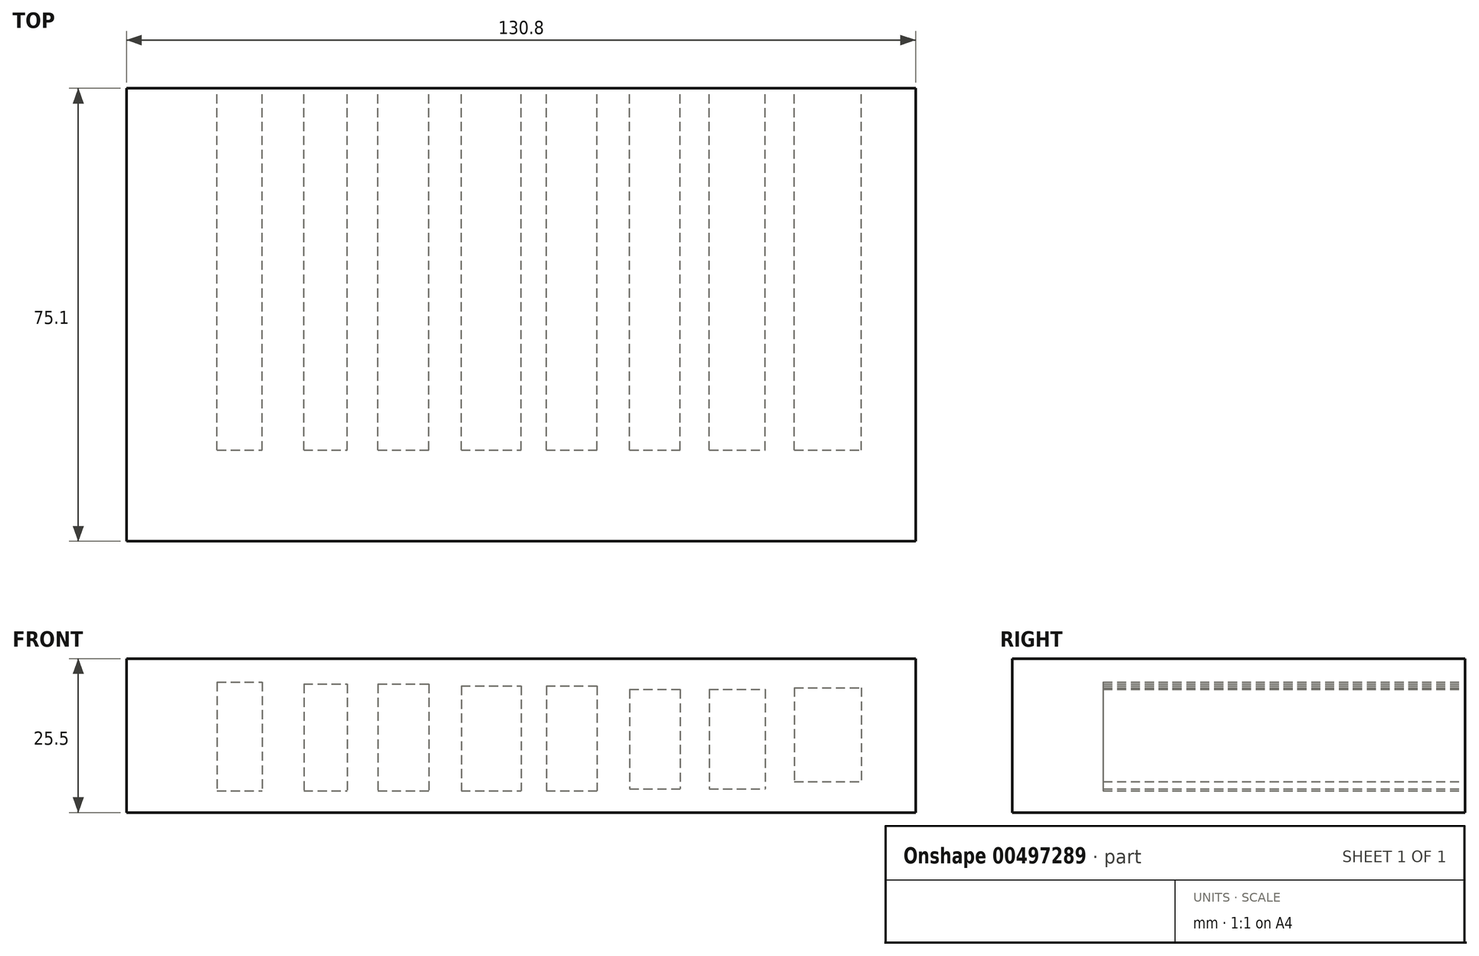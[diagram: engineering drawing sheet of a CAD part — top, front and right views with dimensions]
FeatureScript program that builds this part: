
annotation { "Feature Type Name" : "Feature", "Feature Type Description" : "" }
export const myFeature = defineFeature(function(context is Context, id is Id, definition is map)
    precondition{}
    {
        {
            var Q0;
            Q0=qCreatedBy(makeId("Front.planeOp"),FACE);
            var sketch = newSketch(context, id + "F0", { "sketchPlane" : qUnion([Q0])});
            skLineSegment(sketch, "E0.bottom", {"start": v(65.4, 12.75) * mm, "end": v(-65.4, 12.75) * mm});
            skLineSegment(sketch, "E0.top", {"start": v(65.4, -12.75) * mm, "end": v(-65.4, -12.75) * mm});
            skLineSegment(sketch, "E0.left", {"start": v(65.4, 12.75) * mm, "end": v(65.4, -12.75) * mm});
            skLineSegment(sketch, "E0.right", {"start": v(-65.4, 12.75) * mm, "end": v(-65.4, -12.75) * mm});
            skPoint(sketch, "E0.middle", {"position": v(0, 0) * mm});
            skSolve(sketch);
        }
        {
            var Q0;
            Q0 = qSketchRegion(id + "F0", true);
            extrude(context, id + "F1", {"entities" : qUnion([Q0]), "depth" : 75.1 * mm});
        }
        {
            var Q0;
            Q0=qCreatedBy(makeId("Front.planeOp"),FACE);
            var sketch = newSketch(context, id + "F2", { "sketchPlane" : qUnion([Q0])});
            skLineSegment(sketch, "E1.bottom", {"start": v(-50.4, 8.85) * mm, "end": v(-42.9, 8.85) * mm});
            skLineSegment(sketch, "E1.top", {"start": v(-50.4, -9.15) * mm, "end": v(-42.9, -9.15) * mm});
            skLineSegment(sketch, "E1.left", {"start": v(-50.4, 8.85) * mm, "end": v(-50.4, -9.15) * mm});
            skLineSegment(sketch, "E1.right", {"start": v(-42.9, 8.85) * mm, "end": v(-42.9, -9.15) * mm});
            skLineSegment(sketch, "E2.bottom", {"start": v(-36, 8.55) * mm, "end": v(-28.8, 8.55) * mm});
            skLineSegment(sketch, "E2.top", {"start": v(-36, -9.15) * mm, "end": v(-28.8, -9.15) * mm});
            skLineSegment(sketch, "E2.left", {"start": v(-36, 8.55) * mm, "end": v(-36, -9.15) * mm});
            skLineSegment(sketch, "E2.right", {"start": v(-28.8, 8.55) * mm, "end": v(-28.8, -9.15) * mm});
            skLineSegment(sketch, "E3.bottom", {"start": v(-23.7, 8.55) * mm, "end": v(-15.3, 8.55) * mm});
            skLineSegment(sketch, "E3.top", {"start": v(-23.7, -9.15) * mm, "end": v(-15.3, -9.15) * mm});
            skLineSegment(sketch, "E3.left", {"start": v(-23.7, 8.55) * mm, "end": v(-23.7, -9.15) * mm});
            skLineSegment(sketch, "E3.right", {"start": v(-15.3, 8.55) * mm, "end": v(-15.3, -9.15) * mm});
            skLineSegment(sketch, "E4.bottom", {"start": v(-9.9, 8.25) * mm, "end": v(0, 8.25) * mm});
            skLineSegment(sketch, "E4.top", {"start": v(-9.9, -9.15) * mm, "end": v(0, -9.15) * mm});
            skLineSegment(sketch, "E4.left", {"start": v(-9.9, 8.25) * mm, "end": v(-9.9, -9.15) * mm});
            skLineSegment(sketch, "E4.right", {"start": v(0, 8.25) * mm, "end": v(0, -9.15) * mm});
            skLineSegment(sketch, "E5.bottom", {"start": v(4.2, 8.25) * mm, "end": v(12.6, 8.25) * mm});
            skLineSegment(sketch, "E5.top", {"start": v(4.2, -9.15) * mm, "end": v(12.6, -9.15) * mm});
            skLineSegment(sketch, "E5.left", {"start": v(4.2, 8.25) * mm, "end": v(4.2, -9.15) * mm});
            skLineSegment(sketch, "E5.right", {"start": v(12.6, 8.25) * mm, "end": v(12.6, -9.15) * mm});
            skLineSegment(sketch, "E6.bottom", {"start": v(18, 7.65) * mm, "end": v(26.4, 7.65) * mm});
            skLineSegment(sketch, "E6.top", {"start": v(18, -8.85) * mm, "end": v(26.4, -8.85) * mm});
            skLineSegment(sketch, "E6.left", {"start": v(18, 7.65) * mm, "end": v(18, -8.85) * mm});
            skLineSegment(sketch, "E6.right", {"start": v(26.4, 7.65) * mm, "end": v(26.4, -8.85) * mm});
            skLineSegment(sketch, "E7.bottom", {"start": v(31.2, 7.65) * mm, "end": v(40.5, 7.65) * mm});
            skLineSegment(sketch, "E7.top", {"start": v(31.2, -8.85) * mm, "end": v(40.5, -8.85) * mm});
            skLineSegment(sketch, "E7.left", {"start": v(31.2, 7.65) * mm, "end": v(31.2, -8.85) * mm});
            skLineSegment(sketch, "E7.right", {"start": v(40.5, 7.65) * mm, "end": v(40.5, -8.85) * mm});
            skLineSegment(sketch, "E8.bottom", {"start": v(45.3, 7.95) * mm, "end": v(56.4, 7.95) * mm});
            skLineSegment(sketch, "E8.top", {"start": v(45.3, -7.65) * mm, "end": v(56.4, -7.65) * mm});
            skLineSegment(sketch, "E8.left", {"start": v(45.3, 7.95) * mm, "end": v(45.3, -7.65) * mm});
            skLineSegment(sketch, "E8.right", {"start": v(56.4, 7.95) * mm, "end": v(56.4, -7.65) * mm});
            skSolve(sketch);
        }
        {
            var Q0;
            Q0 = qSketchRegion(id + "F2", true);
            extrude(context, id + "F3", {"entities" : qUnion([Q0]), "operationType" : NewBodyOperationType.REMOVE, "depth" : 60 * mm});
        }
    });
